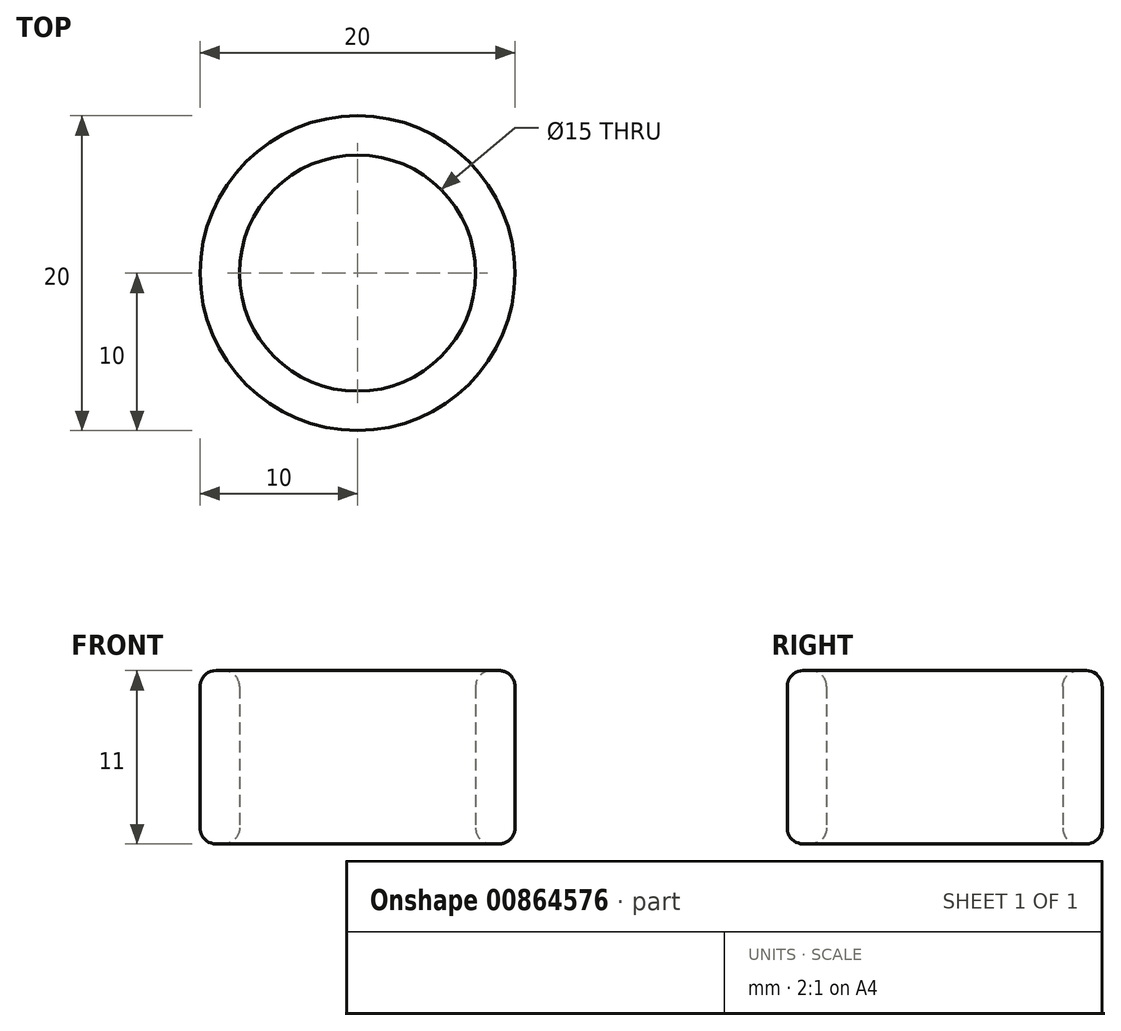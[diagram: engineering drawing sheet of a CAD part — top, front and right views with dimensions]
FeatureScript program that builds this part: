
annotation { "Feature Type Name" : "Feature", "Feature Type Description" : "" }
export const myFeature = defineFeature(function(context is Context, id is Id, definition is map)
    precondition{}
    {
        {
            var Q0;
            Q0=qCreatedBy(makeId("Top.planeOp"),FACE);
            var sketch = newSketch(context, id + "F0", { "sketchPlane" : qUnion([Q0])});
            skCircle(sketch, "E0", {"center": v(0, 0) * mm, "radius": 10 * mm});
            skCircle(sketch, "E1", {"center": v(0, 0) * mm, "radius": 7.5 * mm});
            skSolve(sketch);
        }
        {
            var Q0;
            Q0=makeQuery(id+"F0.imprint","IMPRINT",FACE,{"disambiguationData":[TD([[makeQuery(id+"F0.imprint","IMPRINT",EDGE,{"derivedFrom":sQuery(id+"F0.wireOp",EDGE,"E0")}),1.0]])]});
            extrude(context, id + "F1", {"entities" : qUnion([Q0]), "depth" : 11 * mm, "offsetDistance" : 25 * mm});
        }
        {
            var Q0;
            Q0=makeQuery(id+"F1.opExtrude","SWEPT_FACE",FACE,{"disambiguationData":[OSD([sQuery(id+"F0.wireOp",EDGE,"E1")])]});
            var Q1;
            Q1=makeQuery(id+"F1.opExtrude","CAP_EDGE",EDGE,{"disambiguationData":[OSD([sQuery(id+"F0.wireOp",EDGE,"E0")])],"isStart":false});
            var Q2;
            Q2=makeQuery(id+"F1.opExtrude","CAP_EDGE",EDGE,{"disambiguationData":[OSD([sQuery(id+"F0.wireOp",EDGE,"E0")])],"isStart":true});
            fillet(context, id + "F2", {"entities" : qUnion([Q0, Q1, Q2]), "radius" : 1 * mm, "tangentPropagation" : true, "allowEdgeOverflow" : false});
        }
    });
